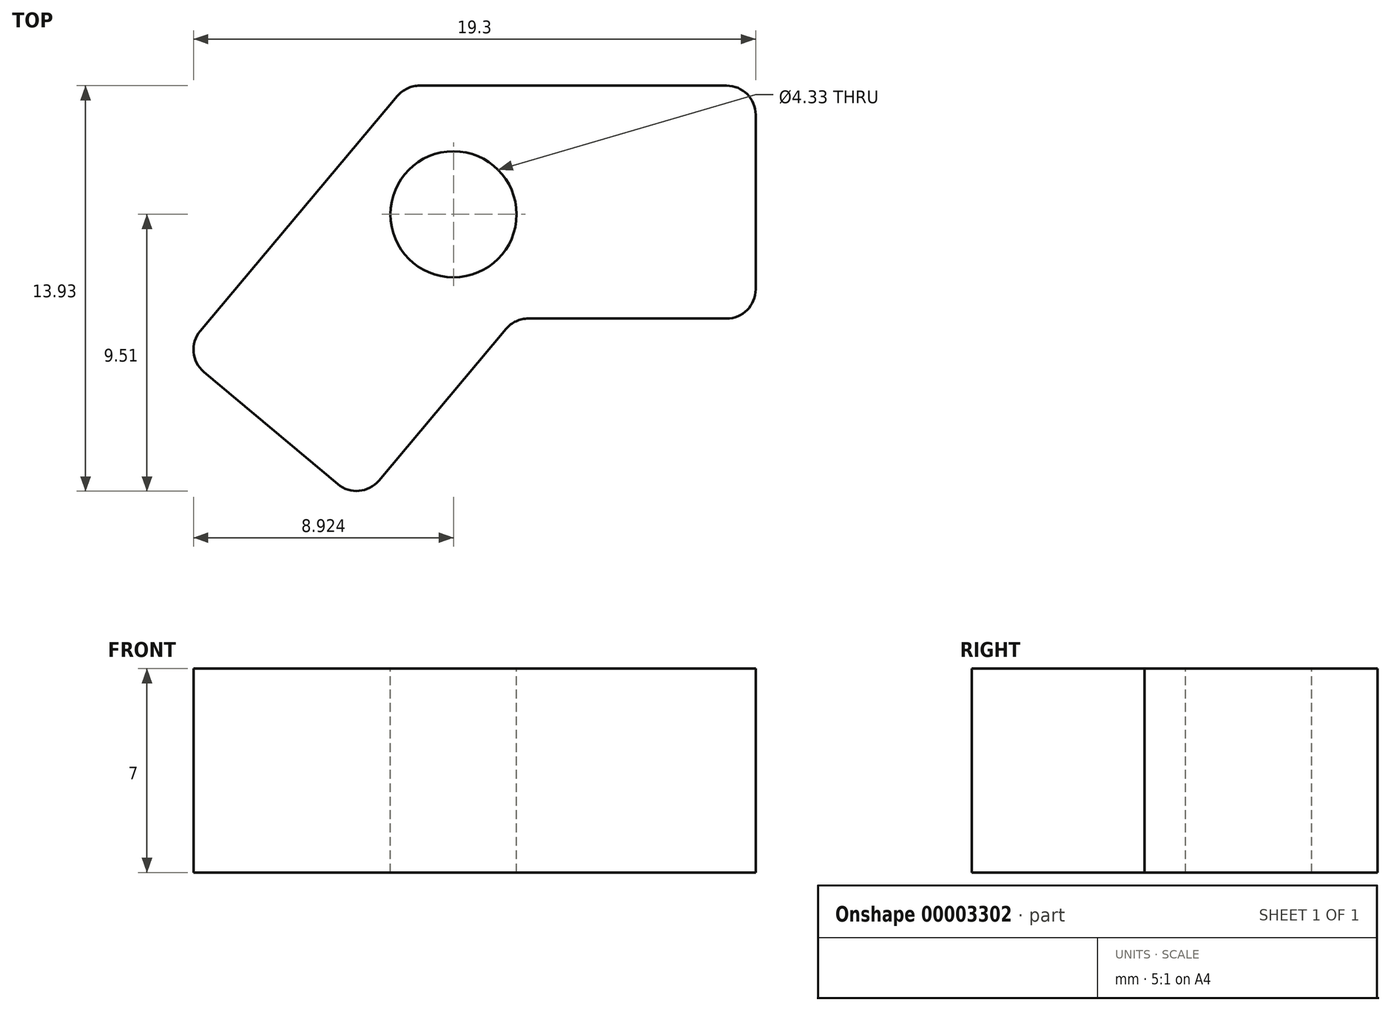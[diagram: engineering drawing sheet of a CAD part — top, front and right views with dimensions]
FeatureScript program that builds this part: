
annotation { "Feature Type Name" : "Feature", "Feature Type Description" : "" }
export const myFeature = defineFeature(function(context is Context, id is Id, definition is map)
    precondition{}
    {
        {
            var Q0;
            Q0=qCreatedBy(makeId("Top.planeOp"),FACE);
            var sketch = newSketch(context, id + "F0", { "sketchPlane" : qUnion([Q0])});
            skLineSegment(sketch, "E0", {"start": v(0, 0) * mm, "end": v(12, 0) * mm});
            skLineSegment(sketch, "E1", {"start": v(12, 0) * mm, "end": v(12, -8) * mm});
            skLineSegment(sketch, "E2", {"start": v(12, -8) * mm, "end": v(3.73, -8) * mm});
            skLineSegment(sketch, "E3", {"start": v(3.73, -8) * mm, "end": v(-1.59, -14.33) * mm});
            skLineSegment(sketch, "E4", {"start": v(-1.59, -14.33) * mm, "end": v(-7.71, -9.2) * mm});
            skLineSegment(sketch, "E5", {"start": v(-7.71, -9.2) * mm, "end": v(0, 0) * mm});
            skSolve(sketch);
        }
        {
            var Q0;
            Q0=makeQuery(id+"F0.imprint","IMPRINT",FACE,{"disambiguationData":[TD([[makeQuery(id+"F0.imprint","IMPRINT",EDGE,{"derivedFrom":sQuery(id+"F0.wireOp",EDGE,"E0")}),-1.0]])]});
            extrude(context, id + "F1", {"entities" : qUnion([Q0]), "depth" : 7 * mm});
        }
        {
            var Q0;
            Q0=makeQuery(id+"F1.opExtrude","SWEPT_EDGE",EDGE,{"disambiguationData":[OSD([sQuery(id+"F0.wireOp",EDGE,"E3"),sQuery(id+"F0.wireOp",EDGE,"E4")])]});
            var Q1;
            Q1=makeQuery(id+"F1.opExtrude","SWEPT_EDGE",EDGE,{"disambiguationData":[OSD([sQuery(id+"F0.wireOp",EDGE,"E2"),sQuery(id+"F0.wireOp",EDGE,"E3")])]});
            var Q2;
            Q2=makeQuery(id+"F1.opExtrude","SWEPT_EDGE",EDGE,{"disambiguationData":[OSD([sQuery(id+"F0.wireOp",EDGE,"E1"),sQuery(id+"F0.wireOp",EDGE,"E2")])]});
            var Q3;
            Q3=makeQuery(id+"F1.opExtrude","SWEPT_EDGE",EDGE,{"disambiguationData":[OSD([sQuery(id+"F0.wireOp",EDGE,"E0"),sQuery(id+"F0.wireOp",EDGE,"E1")])]});
            var Q4;
            Q4=makeQuery(id+"F1.opExtrude","SWEPT_EDGE",EDGE,{"disambiguationData":[OSD([sQuery(id+"F0.wireOp",EDGE,"E4"),sQuery(id+"F0.wireOp",EDGE,"E5")])]});
            var Q5;
            Q5=makeQuery(id+"F1.opExtrude","SWEPT_EDGE",EDGE,{"disambiguationData":[OSD([sQuery(id+"F0.wireOp",EDGE,"E0"),sQuery(id+"F0.wireOp",EDGE,"E5")])]});
            fillet(context, id + "F2", {"entities" : qUnion([Q0, Q1, Q2, Q3, Q4, Q5]), "radius" : 1 * mm, "tangentPropagation" : true, "allowEdgeOverflow" : false});
        }
        {
            var Q0;
            Q0=makeQuery(id+"F1.opExtrude","CAP_FACE",FACE,{"disambiguationData":[OSD([sQuery(id+"F0.wireOp",EDGE,"E0"),sQuery(id+"F0.wireOp",EDGE,"E1"),sQuery(id+"F0.wireOp",EDGE,"E2"),sQuery(id+"F0.wireOp",EDGE,"E3"),sQuery(id+"F0.wireOp",EDGE,"E4"),sQuery(id+"F0.wireOp",EDGE,"E5")])],"isStart":false});
            var sketch = newSketch(context, id + "F3", { "sketchPlane" : qUnion([Q0])});
            skCircle(sketch, "E6", {"center": v(1.62, -4.42) * mm, "radius": 2.16 * mm});
            skSolve(sketch);
        }
        {
            var Q0;
            Q0=makeQuery(id+"F3.imprint","IMPRINT",FACE,{"disambiguationData":[TD([[makeQuery(id+"F3.imprint","IMPRINT",EDGE,{"derivedFrom":sQuery(id+"F3.wireOp",EDGE,"E6")}),1.0]])]});
            extrude(context, id + "F4", {"entities" : qUnion([Q0]), "operationType" : NewBodyOperationType.REMOVE, "oppositeDirection" : true, "depth" : 25 * mm});
        }
    });
